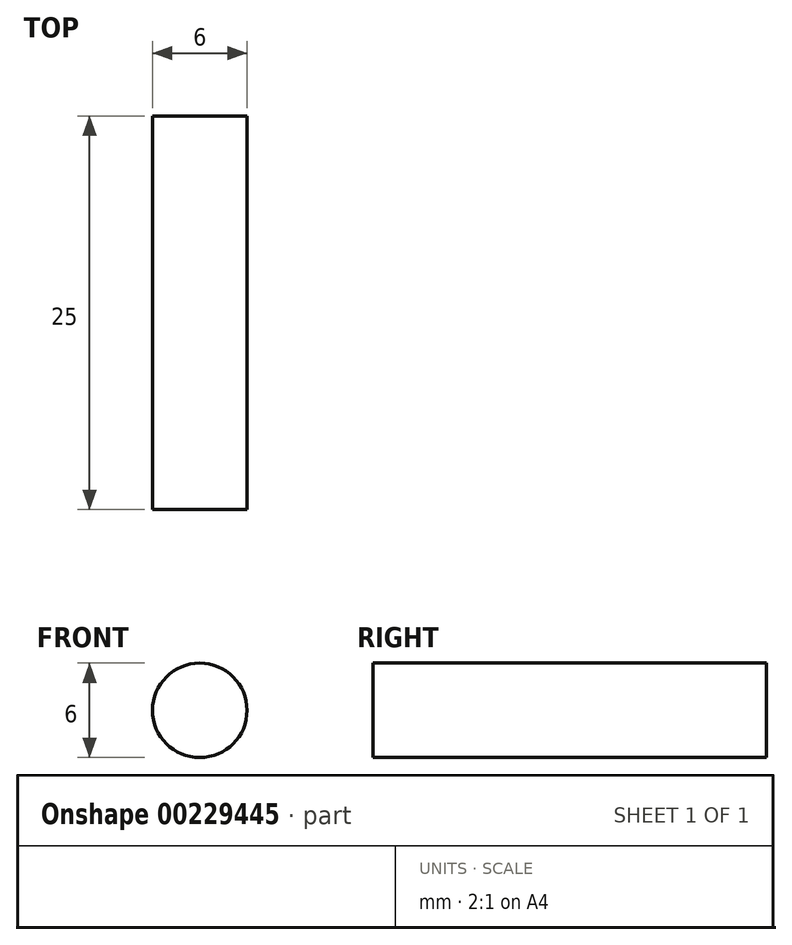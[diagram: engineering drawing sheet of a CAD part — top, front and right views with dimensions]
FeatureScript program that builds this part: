
annotation { "Feature Type Name" : "Feature", "Feature Type Description" : "" }
export const myFeature = defineFeature(function(context is Context, id is Id, definition is map)
    precondition{}
    {
        {
            var Q0;
            Q0=qCreatedBy(makeId("Front.planeOp"),FACE);
            var sketch = newSketch(context, id + "F0", { "sketchPlane" : qUnion([Q0])});
            skCircle(sketch, "E0", {"center": v(0, 0) * mm, "radius": 3 * mm});
            skSolve(sketch);
        }
        {
            var Q0;
            Q0=makeQuery(id+"F0.imprint","IMPRINT",FACE,{"disambiguationData":[TD([[makeQuery(id+"F0.imprint","IMPRINT",EDGE,{"derivedFrom":sQuery(id+"F0.wireOp",EDGE,"E0")}),1.0]])]});
            extrude(context, id + "F1", {"entities" : qUnion([Q0]), "endBound" : BoundingType.SYMMETRIC, "depth" : 25 * mm});
        }
    });
